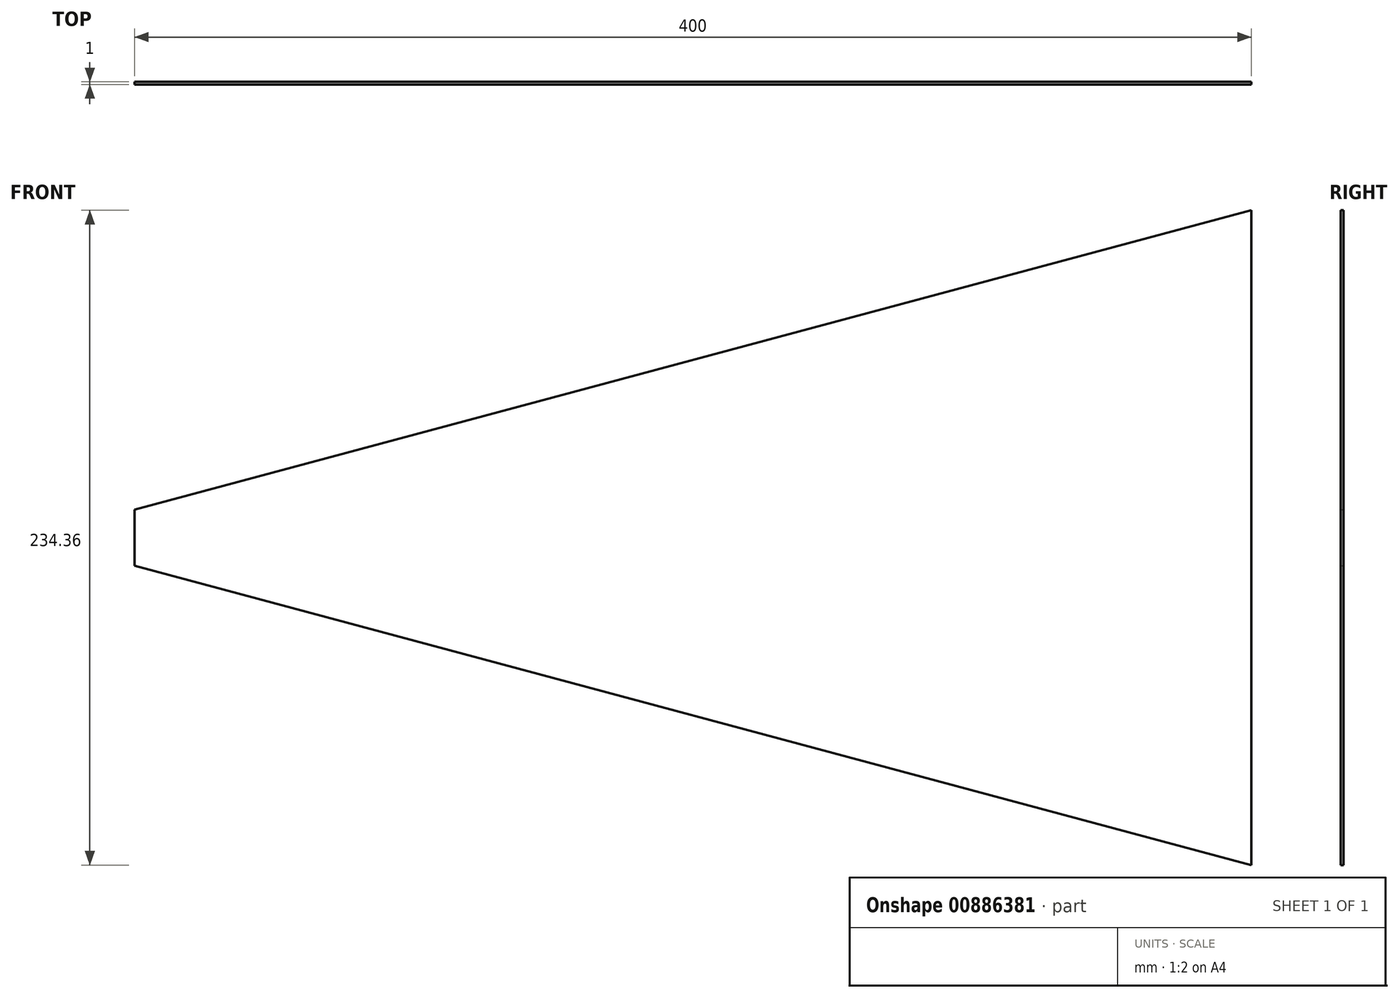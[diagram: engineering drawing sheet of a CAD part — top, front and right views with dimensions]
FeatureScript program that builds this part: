
annotation { "Feature Type Name" : "Feature", "Feature Type Description" : "" }
export const myFeature = defineFeature(function(context is Context, id is Id, definition is map)
    precondition{}
    {
        {
            var Q0;
            Q0=qCreatedBy(makeId("Front.planeOp"),FACE);
            var sketch = newSketch(context, id + "F0", { "sketchPlane" : qUnion([Q0])});
            skLineSegment(sketch, "E0", {"start": v(0, 0) * mm, "end": v(0, 10) * mm});
            skLineSegment(sketch, "E1", {"start": v(0, 10) * mm, "end": v(400, 117.18) * mm});
            skLineSegment(sketch, "E2", {"start": v(400, 117.18) * mm, "end": v(400, 0) * mm});
            skLineSegment(sketch, "E3", {"start": v(400, 0) * mm, "end": v(0, 0) * mm});
            skLineSegment(sketch, "E4.MirrorCS", {"start": v(0, -10) * mm, "end": v(400, -117.18) * mm});
            skLineSegment(sketch, "E5.MirrorCS", {"start": v(0, 0) * mm, "end": v(0, -10) * mm});
            skLineSegment(sketch, "E6.MirrorCS", {"start": v(400, -117.18) * mm, "end": v(400, 0) * mm});
            skSolve(sketch);
        }
        {
            var Q0;
            Q0=makeQuery(id+"F0.imprint","IMPRINT",FACE,{"disambiguationData":[TD([[makeQuery(id+"F0.imprint","IMPRINT",EDGE,{"derivedFrom":sQuery(id+"F0.wireOp",EDGE,"E3")}),1.0]])]});
            var Q1;
            Q1=makeQuery(id+"F0.imprint","IMPRINT",FACE,{"disambiguationData":[TD([[makeQuery(id+"F0.imprint","IMPRINT",EDGE,{"derivedFrom":sQuery(id+"F0.wireOp",EDGE,"E0")}),-1.0]])]});
            extrude(context, id + "F1", {"entities" : qUnion([Q0, Q1]), "depth" : 1 * mm, "offsetDistance" : 25 * mm});
        }
    });
